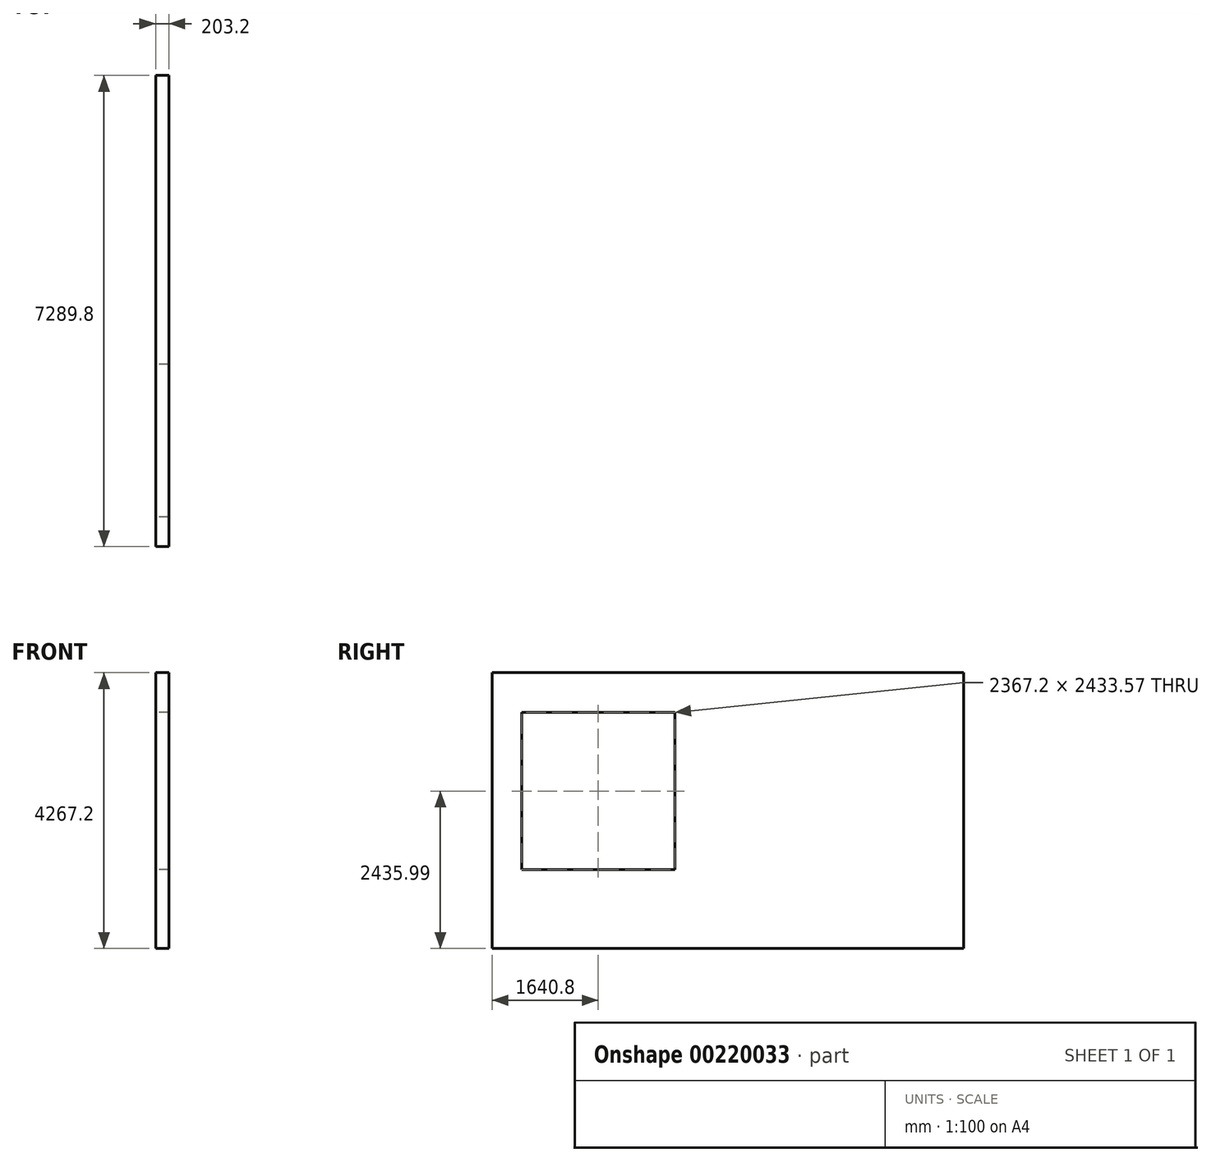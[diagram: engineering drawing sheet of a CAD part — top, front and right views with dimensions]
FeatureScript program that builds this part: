
annotation { "Feature Type Name" : "Feature", "Feature Type Description" : "" }
export const myFeature = defineFeature(function(context is Context, id is Id, definition is map)
    precondition{}
    {
        {
            var Q0;
            Q0=qCreatedBy(makeId("Right.planeOp"),FACE);
            var sketch = newSketch(context, id + "F0", { "sketchPlane" : qUnion([Q0])});
            skLineSegment(sketch, "E0.bottom", {"start": v(0, 0) * mm, "end": v(7289.8, 0) * mm});
            skLineSegment(sketch, "E0.top", {"start": v(0, 4267.2) * mm, "end": v(7289.8, 4267.2) * mm});
            skLineSegment(sketch, "E0.left", {"start": v(0, 0) * mm, "end": v(0, 4267.2) * mm});
            skLineSegment(sketch, "E0.right", {"start": v(7289.8, 0) * mm, "end": v(7289.8, 4267.2) * mm});
            skLineSegment(sketch, "E1.bottom", {"start": v(457.2, 1219.2) * mm, "end": v(2824.4, 1219.2) * mm});
            skLineSegment(sketch, "E1.top", {"start": v(457.2, 3652.77) * mm, "end": v(2824.4, 3652.77) * mm});
            skLineSegment(sketch, "E1.left", {"start": v(457.2, 1219.2) * mm, "end": v(457.2, 3652.77) * mm});
            skLineSegment(sketch, "E1.right", {"start": v(2824.4, 1219.2) * mm, "end": v(2824.4, 3652.77) * mm});
            skSolve(sketch);
        }
        {
            var Q0;
            Q0=makeQuery(id+"F0.imprint","IMPRINT",FACE,{"disambiguationData":[TD([[makeQuery(id+"F0.imprint","IMPRINT",EDGE,{"derivedFrom":sQuery(id+"F0.wireOp",EDGE,"E0.bottom")}),1.0]])]});
            extrude(context, id + "F1", {"entities" : qUnion([Q0]), "depth" : 203.2 * mm});
        }
    });
